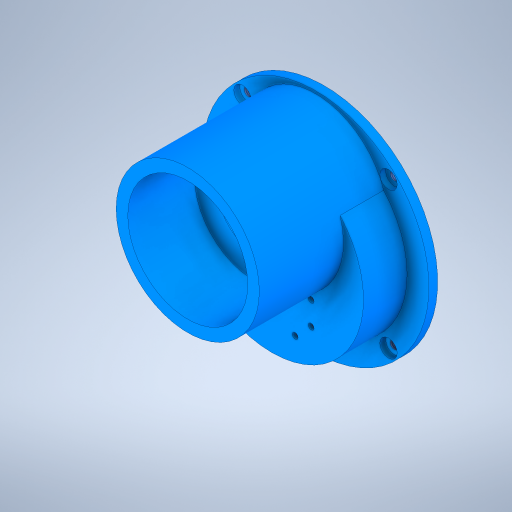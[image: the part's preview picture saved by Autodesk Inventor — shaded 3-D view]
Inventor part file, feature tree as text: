
AUTODESK INVENTOR PART (.ipt)
format: ipt  version: 2024.3 (Build 283343000, 343)  size: 437,760 bytes
history: native  units: mm
features: extrude x8, sketch x5, hole x2, other x1
ambient origin geometry x8: Origin, YZ Plane, XZ Plane, XY Plane, X Axis, Y Axis, Z Axis, Center Point
bodies: Body1 (feature_tree)
feature tree (16):
  other  "Sólido1"
  extrude  "Extrusión1"  Depth=18.0mm TaperAngle=0.0deg
  extrude  "Extrusión2"  Depth=62.0mm
  extrude  "Extrusión3"  Depth=3.0mm
  sketch  "Boceto5"  dims[d2=63.0mm d3=18.0mm d4=0.0mm]
  sketch  "Boceto6"  dims[d5=78.0mm d6=62.0mm]
  extrude  "Extrusión4"  Depth=6.0mm
  hole  "Agujero2"  [1 undecoded]
  extrude  "Extrusión6"  Depth=6.0mm TaperAngle=0.0deg
  hole  "Agujero3"  [1 undecoded]
  extrude  "Extrusión7"  Depth=28.934mm TaperAngle=0.0deg
  extrude  "Extrusión8"  Depth=15.0mm TaperAngle=0.0deg
  extrude  "Extrusión9"  Depth=6.0mm TaperAngle=0.0deg
  sketch  "Boceto7"  dims[d7=3.0mm d8=0.0mm d9=58.0mm]
  sketch  "Boceto8"  dims[d10=6.0mm d11=0.0mm d14=33.75mm]
  sketch  "Boceto9"  dims[d27=32.0mm d28=50.0mm d29=25.0mm d30=11.5mm d31=2.2mm d32=2.2mm d33=2.2mm d34=2.2mm d35=2.2mm d36=2.2mm d37=2.2mm d38=2.2mm d39=2.2mm d40=2.2mm d41=27.0mm d42=16.0mm d43=36.0mm d44=30.5mm d45=6.5mm d46=8.0mm d47=8.0mm d48=8.0mm d49=8.0mm d50=8.0mm d51=8.0mm d52=6.0mm d53=8.307mm d54=22.006mm d55=1.042mm d56=1.042mm d57=11.2mm d58=0.8mm d59=0.8mm d60=0.8mm d61=0.8mm d62=1.75mm d63=0.8mm d64=1.75mm d65=0.8mm d66=3.0mm d67=0.0mm d70=2.013mm d71=5.0mm d72=4.0mm d73=2.0mm d74=90.0deg d75=7.6mm d76=0.0mm d77=6.0mm d78=0.0mm d80=40.0mm d81=78.0mm d82=63.0mm d83=4.0mm d84=2.0mm d85=1.5mm d86=360.0deg d87=4.0mm d88=58.0mm d89=2.85mm d90=7.0mm d91=6.0mm d92=2.0mm d93=90.0deg d94=10.4mm d95=0.0mm d97=49.235mm d98=28.934mm d99=0.0mm d100=15.0mm d101=0.0mm d102=6.0mm d103=0.0mm]
note: 2 required parameter values undecoded (feature->parameter linkage not recoverable at this tier; creation-order binding heuristic only, values carry confidence <= 0.55)
